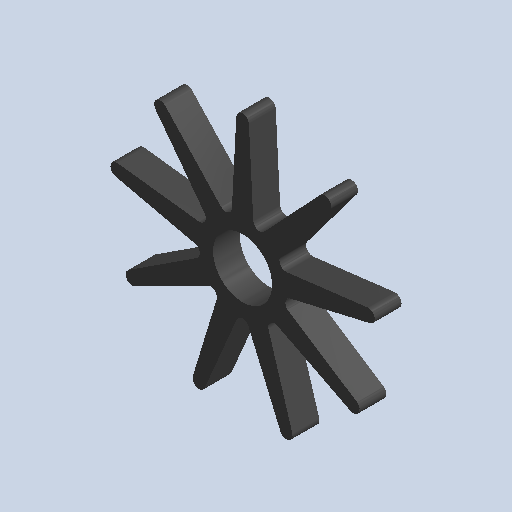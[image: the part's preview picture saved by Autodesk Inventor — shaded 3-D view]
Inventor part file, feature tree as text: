
AUTODESK INVENTOR PART (.ipt)
format: ipt  version: 2022.3 (Build 263350000, 350)  size: 115,712 bytes
history: native  units: mm (DEFAULTED — no unit token found)
features: fillet x1
ambient origin geometry x8: Origin, YZ Plane, XZ Plane, XY Plane, X Axis, Y Axis, Z Axis, Center Point
bodies: Solid1 (feature_tree)
feature tree (1):
  fillet  "Fillet1"  [1 undecoded]
note: 1 required parameter value undecoded (feature->parameter linkage not recoverable at this tier; creation-order binding heuristic only, values carry confidence <= 0.55)
